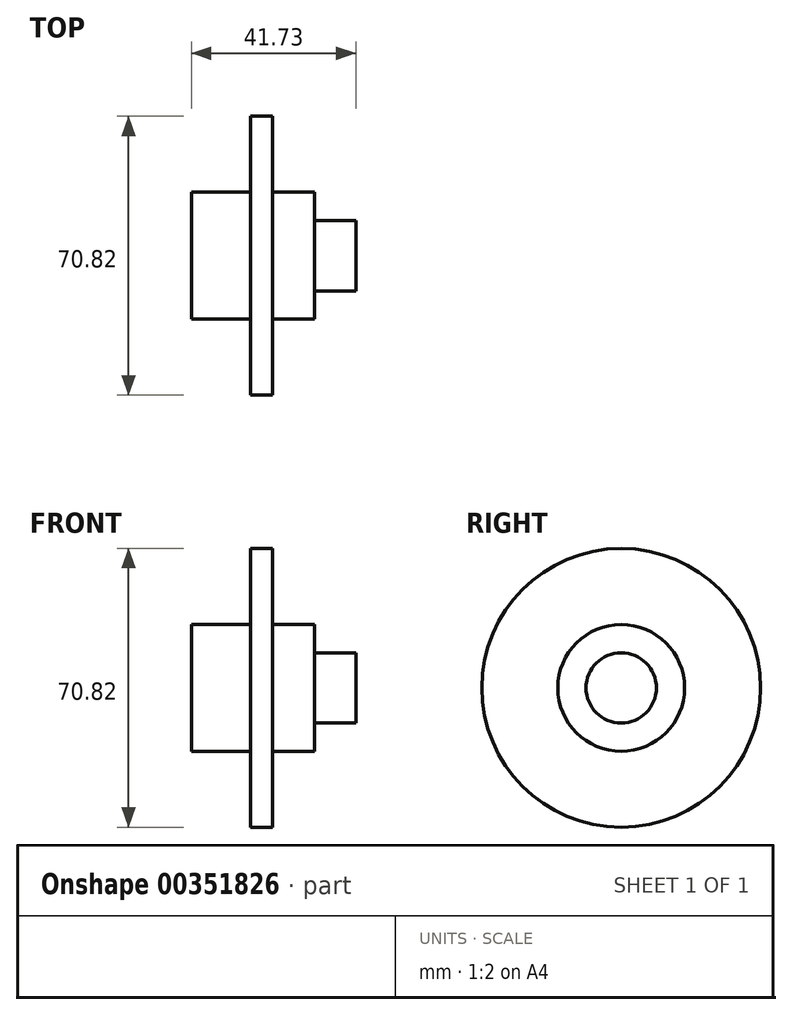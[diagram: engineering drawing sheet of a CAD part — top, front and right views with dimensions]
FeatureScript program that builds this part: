
annotation { "Feature Type Name" : "Feature", "Feature Type Description" : "" }
export const myFeature = defineFeature(function(context is Context, id is Id, definition is map)
    precondition{}
    {
        {
            var Q0;
            Q0=qCreatedBy(makeId("Front.planeOp"),FACE);
            var sketch = newSketch(context, id + "F0", { "sketchPlane" : qUnion([Q0])});
            skLineSegment(sketch, "E0", {"start": v(0, 0) * mm, "end": v(41.73, 0) * mm});
            skLineSegment(sketch, "E1", {"start": v(41.73, 0) * mm, "end": v(41.73, 8.94) * mm});
            skLineSegment(sketch, "E2", {"start": v(41.73, 8.94) * mm, "end": v(31.24, 8.94) * mm});
            skLineSegment(sketch, "E3", {"start": v(31.24, 8.94) * mm, "end": v(31.24, 16.1) * mm});
            skLineSegment(sketch, "E4", {"start": v(31.24, 16.1) * mm, "end": v(20.5, 16.1) * mm});
            skLineSegment(sketch, "E5", {"start": v(20.5, 16.1) * mm, "end": v(20.5, 35.41) * mm});
            skLineSegment(sketch, "E6", {"start": v(20.5, 35.41) * mm, "end": v(15.02, 35.41) * mm});
            skLineSegment(sketch, "E7", {"start": v(15.02, 35.41) * mm, "end": v(15.02, 16.1) * mm});
            skLineSegment(sketch, "E8", {"start": v(15.02, 16.1) * mm, "end": v(0, 16.1) * mm});
            skLineSegment(sketch, "E9", {"start": v(0, 16.1) * mm, "end": v(0, 0) * mm});
            skSolve(sketch);
        }
        {
            var Q0;
            Q0=makeQuery(id+"F0.imprint","IMPRINT",FACE,{"disambiguationData":[TD([[makeQuery(id+"F0.imprint","IMPRINT",EDGE,{"derivedFrom":sQuery(id+"F0.wireOp",EDGE,"E0")}),1.0]])]});
            var Q1;
            Q1=sQuery(id+"F0.wireOp",EDGE,"E0");
            revolve(context, id + "F1", {"entities" : qUnion([Q0]), "axis" : qUnion([Q1]), "revolveType" : RevolveType.FULL});
        }
    });
